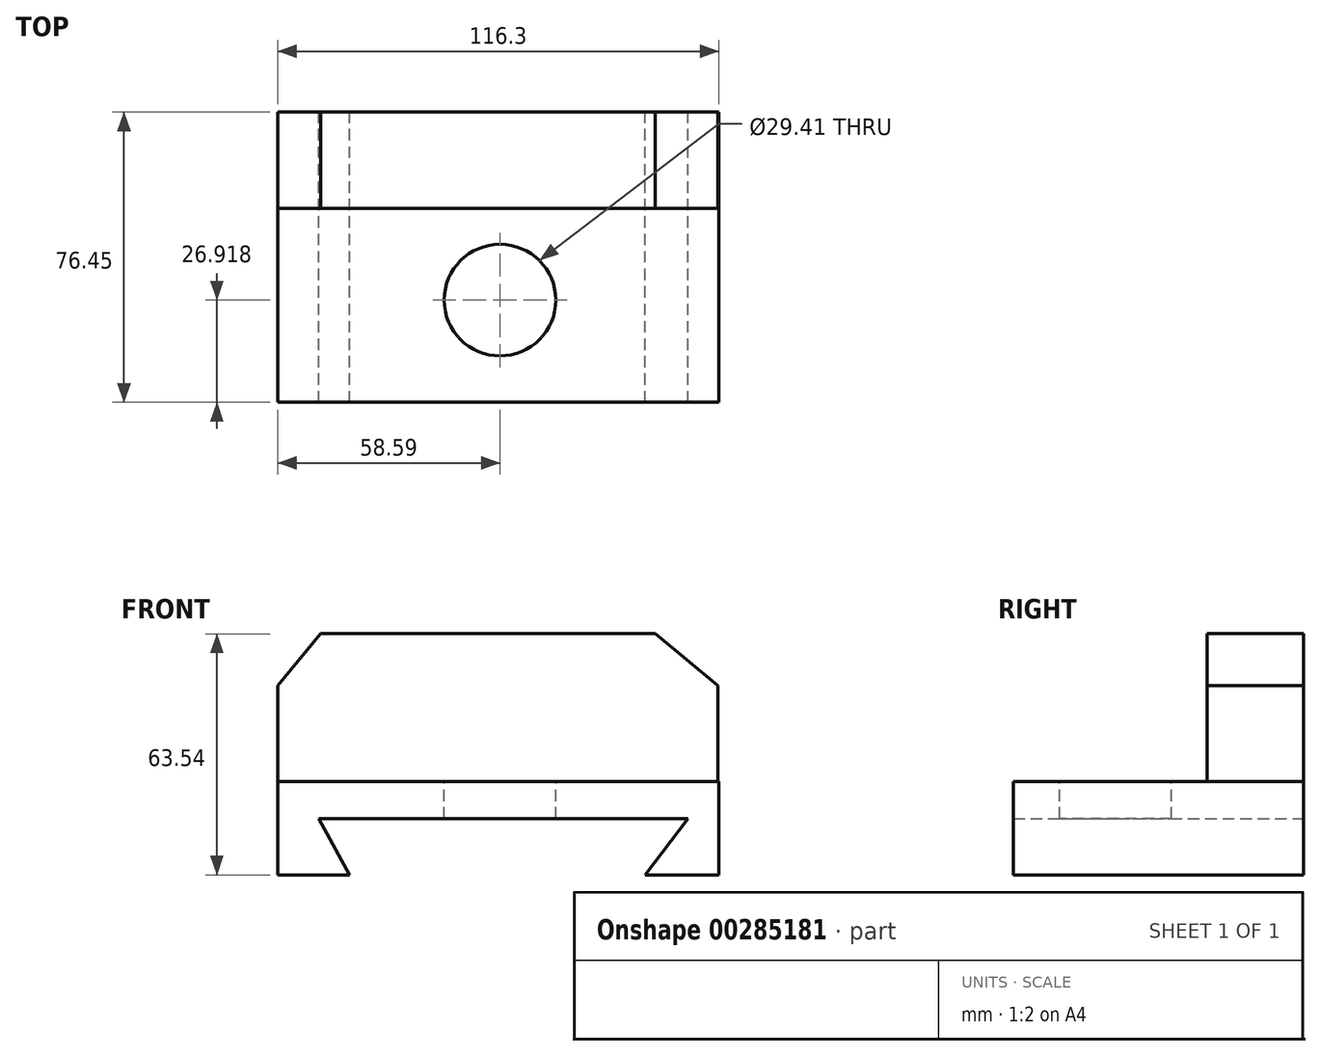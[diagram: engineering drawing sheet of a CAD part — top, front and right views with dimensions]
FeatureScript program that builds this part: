
annotation { "Feature Type Name" : "Feature", "Feature Type Description" : "" }
export const myFeature = defineFeature(function(context is Context, id is Id, definition is map)
    precondition{}
    {
        {
            var Q0;
            Q0=qCreatedBy(makeId("Front.planeOp"),FACE);
            var sketch = newSketch(context, id + "F0", { "sketchPlane" : qUnion([Q0])});
            skLineSegment(sketch, "E0", {"start": v(-58.59, 0) * mm, "end": v(57.71, 0) * mm});
            skLineSegment(sketch, "E1", {"start": v(57.71, 0) * mm, "end": v(57.71, -24.63) * mm});
            skLineSegment(sketch, "E2", {"start": v(57.71, -24.63) * mm, "end": v(38.18, -24.63) * mm});
            skLineSegment(sketch, "E3", {"start": v(38.18, -24.63) * mm, "end": v(49.55, -9.76) * mm});
            skLineSegment(sketch, "E4", {"start": v(-58.59, 0) * mm, "end": v(-58.59, -24.63) * mm});
            skPoint(sketch, "E4.endSnap0", {"position": v(47.95, -24.63) * mm});
            skLineSegment(sketch, "E5", {"start": v(-58.59, -24.63) * mm, "end": v(-39.64, -24.63) * mm});
            skLineSegment(sketch, "E6", {"start": v(-39.64, -24.63) * mm, "end": v(-47.8, -9.76) * mm});
            skLineSegment(sketch, "E7", {"start": v(-47.8, -9.76) * mm, "end": v(49.55, -9.76) * mm});
            skSolve(sketch);
        }
        {
            var Q0;
            Q0 = qSketchRegion(id + "F0", true);
            extrude(context, id + "F1", {"entities" : qUnion([Q0]), "depth" : 76.45 * mm});
        }
        {
            var Q0;
            Q0=qCreatedBy(makeId("Front.planeOp"),FACE);
            var sketch = newSketch(context, id + "F2", { "sketchPlane" : qUnion([Q0])});
            skLineSegment(sketch, "E8", {"start": v(-58.59, 0) * mm, "end": v(-58.59, 25.21) * mm});
            skLineSegment(sketch, "E9", {"start": v(-58.59, 25.21) * mm, "end": v(-47.22, 38.91) * mm});
            skLineSegment(sketch, "E10", {"start": v(57.42, 0) * mm, "end": v(57.42, 25.21) * mm});
            skLineSegment(sketch, "E11", {"start": v(57.42, 25.21) * mm, "end": v(40.91, 38.91) * mm});
            skLineSegment(sketch, "E12", {"start": v(40.91, 38.91) * mm, "end": v(-47.22, 38.91) * mm});
            skLineSegment(sketch, "E13", {"start": v(-58.59, 0) * mm, "end": v(57.42, 0) * mm});
            skSolve(sketch);
        }
        {
            var Q0;
            Q0 = qSketchRegion(id + "F2", true);
            extrude(context, id + "F3", {"entities" : qUnion([Q0]), "operationType" : NewBodyOperationType.ADD, "depth" : 25.4 * mm});
        }
        {
            var Q0;
            Q0=qCreatedBy(makeId("Top.planeOp"),FACE);
            var sketch = newSketch(context, id + "F4", { "sketchPlane" : qUnion([Q0])});
            skCircle(sketch, "E14", {"center": v(0, -49.53) * mm, "radius": 14.7 * mm});
            skSolve(sketch);
        }
        {
            var Q0;
            Q0 = qSketchRegion(id + "F4", true);
            extrude(context, id + "F5", {"entities" : qUnion([Q0]), "operationType" : NewBodyOperationType.REMOVE, "oppositeDirection" : true, "depth" : 25.4 * mm});
        }
    });
